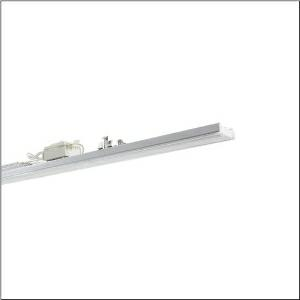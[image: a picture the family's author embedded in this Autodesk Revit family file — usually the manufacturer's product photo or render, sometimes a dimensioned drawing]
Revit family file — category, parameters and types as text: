
# Revit family: licross_r__11_recessed_ho_51tl12dn4exmd_9a02
name_source: partatom
category: Lighting Fixtures
units: mm (PartAtom-declared; Revit-internal decimal feet)

## family parameters
Cut with Voids When Loaded = No
Host = Face
Light Source = No
Part Type = Normal
Room Calculation Point = No
Round Connector Dimension = Use Diameter
Shared = No

## types (1)
- --- (1 x LED, 2110 lm, 12.6 W, 4000K)
    Apparent Load = 13 VA
    CIE Flux Codes = 66 91 98 100 100
    Color Rendering = 80
    Color Temperature = 4000K
    Default Elevation = 1800 mm
    Description = Licross® 11 Recessed HO, luminaire insert, of sheet steel, coil coated, white, length: 1.500mm, width: 66mm, height: 67mm, LED rated luminous flux: 14.030lm, light colour: 840, control gear: DALI 2 (for two DALI lines), with plug, 6-pole, with phase selection, mains connection: 220..240V, AC/DC, 0/50..60Hz, rated input power: 77W, without changeover relay, for emergency light function, for central battery installations according to DIN EN 60598-2-22, halogen-free wiring, primary optical cover: cover, of PMMA, light emission: direct distribution, primary light characteristic: symmetric, protection rating (complete): IP40, insulation class (complete): insulation class I (protective earthing), certification: CE, ENEC, VDE, UKCA, protection symbol: D if used in an environment without relevant dust loads with corresponding accessories, impact resistance: IK06, permissible ambient temperature for indoor applications: -25..+30°C, standard: EN 60598-2-22, corresponds to IFS (International Featured Standards) requirements for safety and quality in the food industry, reducing of maximum allowable ambient temperature of 5°C with ceiling mounting, LABS conformity tested according to VDMA 24364:2018-05, packaging unit: 1 piece
    Height = 58 mm
    Lamp = 1 x LED
    Lamp Light Flux = 2110 lm
    Lamp Power = 12.6 W
    Lamp count = 1
    Length = 1500 mm
    Luminous efficacy = 167 lm/W
    Manufacturer = Siteco
    ModVariant = No
    Model = 51TL12DN4EXMD
    Mounting Place = Ceiling
    Mounting Type = Pendant
    Number of Poles = 1
    OnlyDefault = Yes
    Power Factor = 1
    Product Name = Licross® 11 Recessed HO
    Product group = luminaire insert
    ProductGroupID = 902
    Protection Class = Protection class I
    Protection Degree = IP 40
    RLX_Detail_Level = 1
    RLX_Emergency_Light_Flux = 0 lm
    RLX_Emergency_Type = 0
    RLX_Emergency_Type_DB = No
    RlxData = <blob elided: 25029 chars, md5=f6bc7746>
    Socket = socket
    Standby Power = 0 W
    System Light Flux = 2110 lm
    System Power = 13 W
    Type Comments = : DC mode (central or group accumulator) initial emergency light level
    Type Image = l_1296930.jpg
    URL = http://relux.com
    VarID = @adj_087260
    Voltage = 0 V
    Weight = 0.00 kg
    Width = 66 mm

## geometry (parser evidence)
native form markers: Blend x4, Sweep x10
no freeform markers — native parametric forms only
